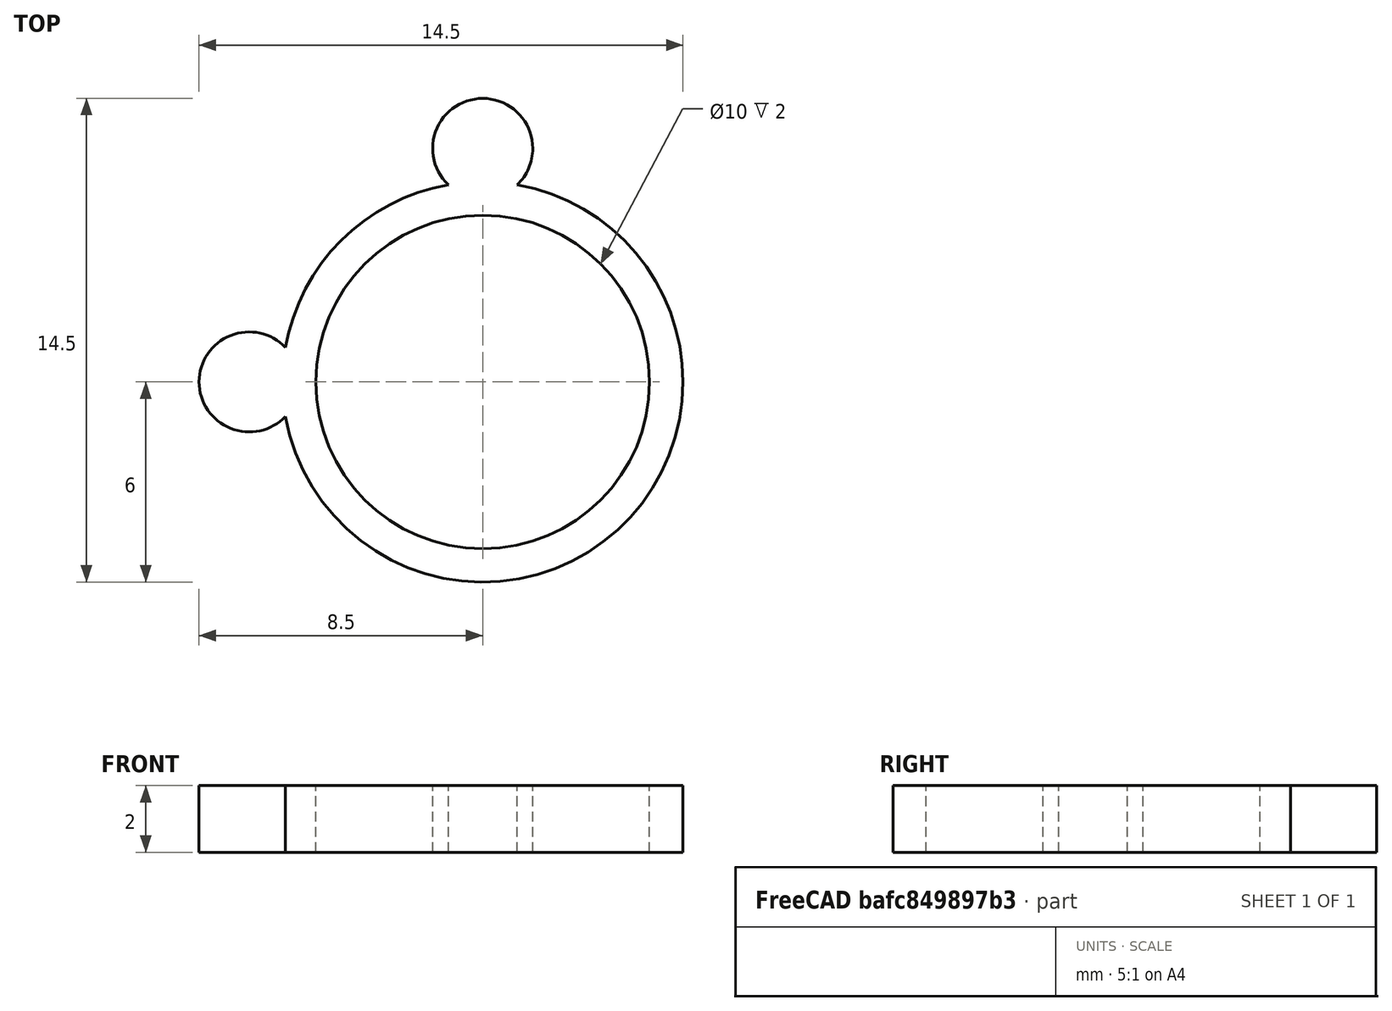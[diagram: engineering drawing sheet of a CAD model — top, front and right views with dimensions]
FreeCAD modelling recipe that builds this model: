
FCSTD DOCUMENT  (FreeCAD 0.19R24291 (Git))
Label: reto6
License: All rights reserved
LicenseURL: http://en.wikipedia.org/wiki/All_rights_reserved
objects: Part::Cylinder×4, Part::Cut×1, Part::MultiFuse×1
note: 6 computed .brp shape members not serialized (recipe doc carries the construction recipe); baked Part::Feature solids carry a one-line shape summary decoded from their .brp

FEATURE [Part::Cylinder] Cylinder
  Angle = 360
  AttacherType = Attacher::AttachEngine3D
  Height = 2
  Radius = 6
FEATURE [Part::Cylinder] Cylinder001
  Angle = 360
  AttacherType = Attacher::AttachEngine3D
  Height = 3
  Radius = 5
FEATURE [Part::Cut] Cut
  Base = -> Cylinder
  Refine = true
  Tool = -> Cylinder001
FEATURE [Part::Cylinder] Cylinder002
  Angle = 360
  AttacherType = Attacher::AttachEngine3D
  Height = 2
  Placement = pos=(-7,0,0) rot=(0,0,1;0rad)
  Radius = 1.5
FEATURE [Part::Cylinder] Cylinder003
  Angle = 360
  AttacherType = Attacher::AttachEngine3D
  Height = 2
  Placement = pos=(0,7,0) rot=(0,0,1;0rad)
  Radius = 1.5
FEATURE [Part::MultiFuse] Fusion
  Refine = true
  Shapes = -> [Cylinder002,Cylinder003,Cut]
